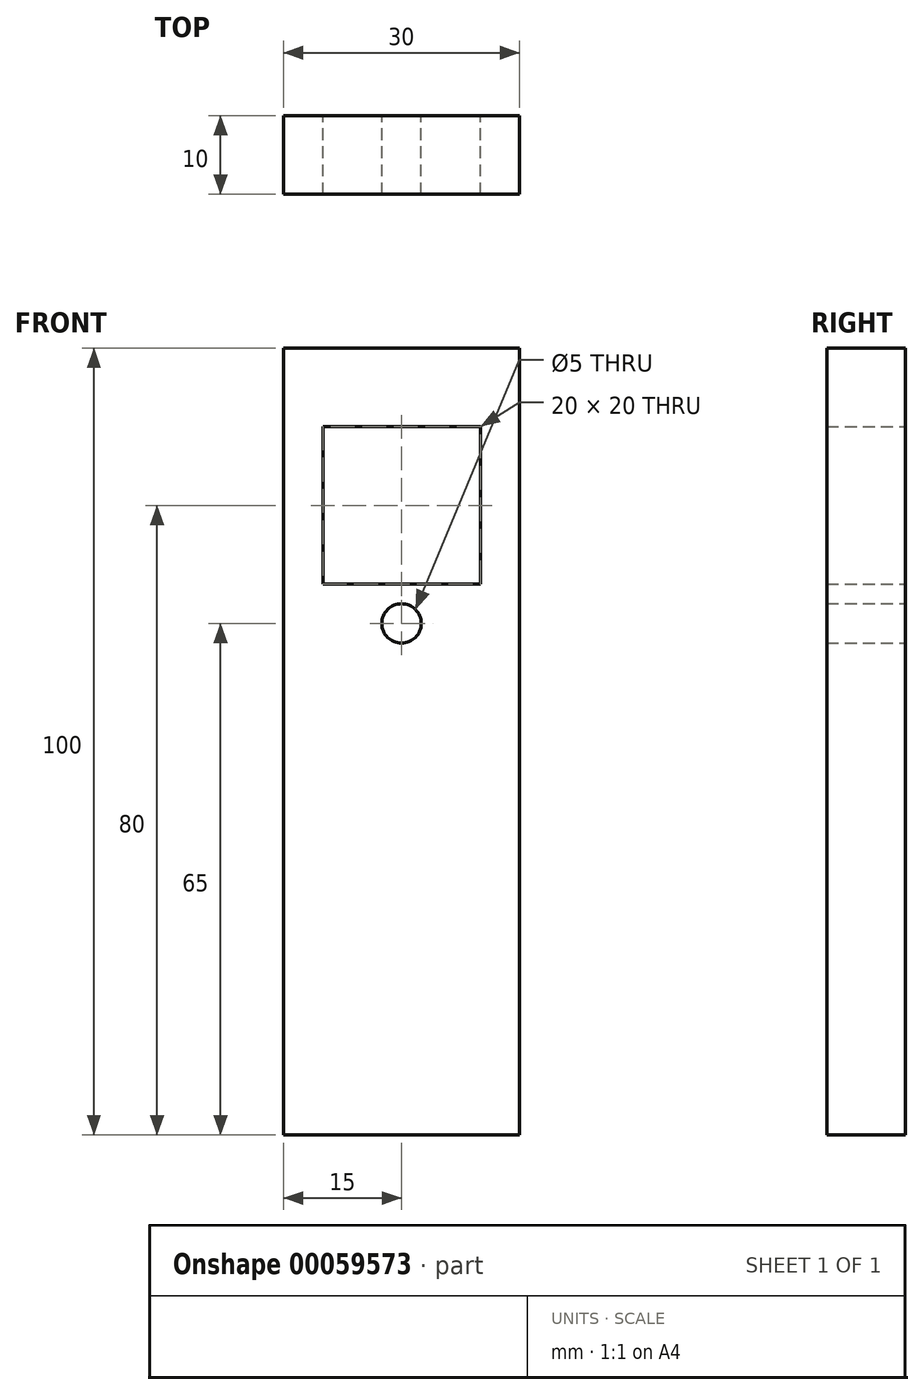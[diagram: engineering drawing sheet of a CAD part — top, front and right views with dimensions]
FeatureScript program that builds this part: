
annotation { "Feature Type Name" : "Feature", "Feature Type Description" : "" }
export const myFeature = defineFeature(function(context is Context, id is Id, definition is map)
    precondition{}
    {
        {
            var Q0;
            Q0=qCreatedBy(makeId("Front.planeOp"),FACE);
            var sketch = newSketch(context, id + "F0", { "sketchPlane" : qUnion([Q0])});
            skLineSegment(sketch, "E0.rect.bottom", {"start": v(-15, 50) * mm, "end": v(15, 50) * mm});
            skLineSegment(sketch, "E0.rect.top", {"start": v(-15, -50) * mm, "end": v(15, -50) * mm});
            skLineSegment(sketch, "E0.rect.left", {"start": v(-15, 50) * mm, "end": v(-15, -50) * mm});
            skLineSegment(sketch, "E0.rect.right", {"start": v(15, 50) * mm, "end": v(15, -50) * mm});
            skPoint(sketch, "E0.rect.middle", {"position": v(0, 0) * mm});
            skLineSegment(sketch, "E1.rect.bottom", {"start": v(-10, 40) * mm, "end": v(10, 40) * mm});
            skLineSegment(sketch, "E1.rect.top", {"start": v(-10, 20) * mm, "end": v(10, 20) * mm});
            skLineSegment(sketch, "E1.rect.left", {"start": v(-10, 40) * mm, "end": v(-10, 20) * mm});
            skLineSegment(sketch, "E1.rect.right", {"start": v(10, 40) * mm, "end": v(10, 20) * mm});
            skPoint(sketch, "E1.rect.middle", {"position": v(0, 30) * mm});
            skCircle(sketch, "E2", {"center": v(0, 15) * mm, "radius": 2.5 * mm});
            skSolve(sketch);
        }
        {
            var Q0;
            Q0 = qSketchRegion(id + "F0", true);
            extrude(context, id + "F1", {"entities" : qUnion([Q0]), "depth" : 10 * mm});
        }
    });
